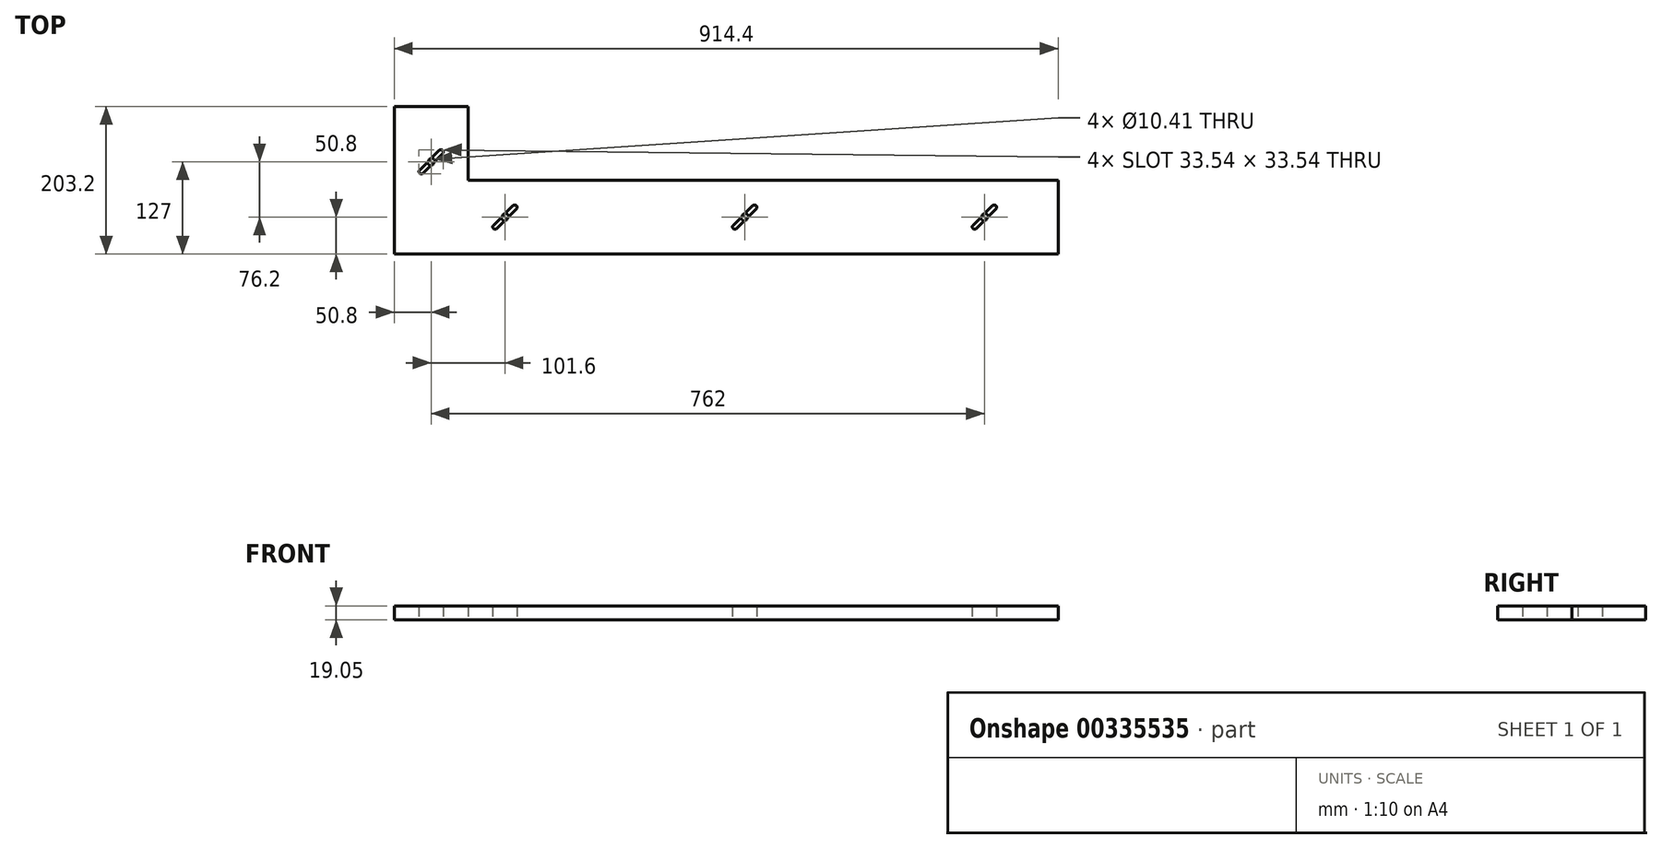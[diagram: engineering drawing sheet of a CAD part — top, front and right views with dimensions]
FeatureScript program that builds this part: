
annotation { "Feature Type Name" : "Feature", "Feature Type Description" : "" }
export const myFeature = defineFeature(function(context is Context, id is Id, definition is map)
    precondition{}
    {
        {
            var Q0;
            Q0=qCreatedBy(makeId("Top.planeOp"),FACE);
            var sketch = newSketch(context, id + "F0", { "sketchPlane" : qUnion([Q0])});
            skLineSegment(sketch, "E0.bottom", {"start": v(0, 203.2) * mm, "end": v(101.6, 203.2) * mm});
            skLineSegment(sketch, "E0.top", {"start": v(0, 0) * mm, "end": v(914.4, 0) * mm});
            skLineSegment(sketch, "E0.left", {"start": v(0, 203.2) * mm, "end": v(0, 0) * mm});
            skLineSegment(sketch, "E0.right", {"start": v(914.4, 101.6) * mm, "end": v(914.4, 0) * mm});
            skLineSegment(sketch, "E1", {"start": v(101.6, 101.6) * mm, "end": v(101.6, 203.2) * mm});
            skLineSegment(sketch, "E2", {"start": v(914.4, 101.6) * mm, "end": v(101.6, 101.6) * mm});
            skLineSegment(sketch, "E3", {"start": v(50.8, 203.2) * mm, "end": v(50.8, 50.8) * mm, "construction": true});
            skLineSegment(sketch, "E4", {"start": v(914.4, 50.8) * mm, "end": v(50.8, 50.8) * mm, "construction": true});
            skCircle(sketch, "E5", {"center": v(50.8, 127) * mm, "radius": 5.2 * mm});
            skCircle(sketch, "E6", {"center": v(152.4, 50.8) * mm, "radius": 5.2 * mm});
            skCircle(sketch, "E7", {"center": v(812.8, 50.8) * mm, "radius": 5.2 * mm});
            skCircle(sketch, "E8", {"center": v(482.6, 50.8) * mm, "radius": 5.2 * mm});
            skSolve(sketch);
        }
        {
            var Q0;
            Q0=makeQuery(id+"F0.imprint","IMPRINT",FACE,{"disambiguationData":[TD([[makeQuery(id+"F0.imprint","IMPRINT",EDGE,{"derivedFrom":sQuery(id+"F0.wireOp",EDGE,"E0.bottom")}),-1.0]])]});
            var sketch = newSketch(context, id + "F1", { "sketchPlane" : qUnion([Q0])});
            skPoint(sketch, "E9.0", {"position": v(0, 203.2) * mm});
            skPoint(sketch, "E10.0", {"position": v(101.6, 203.2) * mm});
            skPoint(sketch, "E11.0", {"position": v(101.6, 101.6) * mm});
            skPoint(sketch, "E12.0", {"position": v(914.4, 101.6) * mm});
            skPoint(sketch, "E13.0", {"position": v(914.4, 0) * mm});
            skPoint(sketch, "E14.0", {"position": v(0, 0) * mm});
            skPoint(sketch, "E15.0", {"position": v(50.8, 127) * mm});
            skPoint(sketch, "E16.0", {"position": v(152.4, 50.8) * mm});
            skPoint(sketch, "E17.0", {"position": v(482.6, 50.8) * mm});
            skPoint(sketch, "E18.0", {"position": v(812.8, 50.8) * mm});
            skLineSegment(sketch, "E19", {"start": v(0, 203.2) * mm, "end": v(101.6, 203.2) * mm});
            skLineSegment(sketch, "E20", {"start": v(101.6, 203.2) * mm, "end": v(101.6, 101.6) * mm});
            skLineSegment(sketch, "E21", {"start": v(101.6, 101.6) * mm, "end": v(914.4, 101.6) * mm});
            skLineSegment(sketch, "E22", {"start": v(914.4, 101.6) * mm, "end": v(914.4, 0) * mm});
            skLineSegment(sketch, "E23", {"start": v(914.4, 0) * mm, "end": v(0, 0) * mm});
            skLineSegment(sketch, "E24", {"start": v(0, 0) * mm, "end": v(0, 203.2) * mm});
            skLineSegment(sketch, "E25", {"start": v(39.66, 111.2) * mm, "end": v(66.6, 138.14) * mm});
            skLineSegment(sketch, "E26", {"start": v(39.66, 111.2) * mm, "end": v(66.6, 111.2) * mm, "construction": true});
            skLineSegment(sketch, "E27", {"start": v(35, 115.86) * mm, "end": v(61.94, 142.8) * mm});
            skArc(sketch, "E28", {"start": v(66.6, 138.14) * mm, "mid": v(66.6, 142.8) * mm, "end": v(61.94, 142.8) * mm});
            skArc(sketch, "E29", {"start": v(35, 115.86) * mm, "mid": v(35, 111.2) * mm, "end": v(39.66, 111.2) * mm});
            skLineSegment(sketch, "E30", {"start": v(37.33, 113.53) * mm, "end": v(64.27, 140.47) * mm, "construction": true});
            skLineSegment(sketch, "E31", {"start": v(66.6, 138.14) * mm, "end": v(66.6, 111.2) * mm, "construction": true});
            skLineSegment(sketch, "E32", {"start": v(141.26, 35) * mm, "end": v(168.2, 61.94) * mm});
            skLineSegment(sketch, "E33", {"start": v(141.26, 35) * mm, "end": v(168.2, 35) * mm, "construction": true});
            skLineSegment(sketch, "E34", {"start": v(136.6, 39.66) * mm, "end": v(163.54, 66.6) * mm});
            skArc(sketch, "E35", {"start": v(168.2, 61.94) * mm, "mid": v(168.2, 66.6) * mm, "end": v(163.54, 66.6) * mm});
            skArc(sketch, "E36", {"start": v(136.6, 39.66) * mm, "mid": v(136.6, 35) * mm, "end": v(141.26, 35) * mm});
            skLineSegment(sketch, "E37", {"start": v(138.93, 37.33) * mm, "end": v(165.87, 64.27) * mm, "construction": true});
            skLineSegment(sketch, "E38", {"start": v(168.2, 61.94) * mm, "end": v(168.2, 35) * mm, "construction": true});
            skLineSegment(sketch, "E39", {"start": v(471.46, 35) * mm, "end": v(498.4, 61.94) * mm});
            skLineSegment(sketch, "E40", {"start": v(471.46, 35) * mm, "end": v(498.4, 35) * mm, "construction": true});
            skLineSegment(sketch, "E41", {"start": v(466.8, 39.66) * mm, "end": v(493.74, 66.6) * mm});
            skArc(sketch, "E42", {"start": v(498.4, 61.94) * mm, "mid": v(498.4, 66.6) * mm, "end": v(493.74, 66.6) * mm});
            skArc(sketch, "E43", {"start": v(466.8, 39.66) * mm, "mid": v(466.8, 35) * mm, "end": v(471.46, 35) * mm});
            skLineSegment(sketch, "E44", {"start": v(469.13, 37.33) * mm, "end": v(496.07, 64.27) * mm, "construction": true});
            skLineSegment(sketch, "E45", {"start": v(498.4, 61.94) * mm, "end": v(498.4, 35) * mm, "construction": true});
            skLineSegment(sketch, "E46", {"start": v(801.66, 35) * mm, "end": v(828.6, 61.94) * mm});
            skLineSegment(sketch, "E47", {"start": v(801.66, 35) * mm, "end": v(828.6, 35) * mm, "construction": true});
            skLineSegment(sketch, "E48", {"start": v(797, 39.66) * mm, "end": v(823.94, 66.6) * mm});
            skArc(sketch, "E49", {"start": v(828.6, 61.94) * mm, "mid": v(828.6, 66.6) * mm, "end": v(823.94, 66.6) * mm});
            skArc(sketch, "E50", {"start": v(797, 39.66) * mm, "mid": v(797, 35) * mm, "end": v(801.66, 35) * mm});
            skLineSegment(sketch, "E51", {"start": v(799.33, 37.33) * mm, "end": v(826.27, 64.27) * mm, "construction": true});
            skLineSegment(sketch, "E52", {"start": v(828.6, 61.94) * mm, "end": v(828.6, 35) * mm, "construction": true});
            skSolve(sketch);
        }
        {
            var Q0;
            Q0 = qSketchRegion(id + "F1", true);
            extrude(context, id + "F2", {"entities" : qUnion([Q0]), "depth" : 19.05 * mm, "offsetDistance" : 25.4 * mm});
        }
        {
            var Q0;
            Q0=makeQuery(id+"F0.imprint","IMPRINT",FACE,{"disambiguationData":[TD([[makeQuery(id+"F0.imprint","IMPRINT",EDGE,{"derivedFrom":sQuery(id+"F0.wireOp",EDGE,"E0.bottom")}),-1.0]])]});
            extrude(context, id + "F3", {"entities" : qUnion([Q0]), "depth" : 5 / 203.2 * mm, "offsetDistance" : 25.4 * mm});
        }
    });
